# Revit family: Dimension Lumber
name_source: partatom
category: Structural Framing
revit_build: Autodesk Revit Architecture 2012 (Build: 20110210_1515)
units: mm (PartAtom-declared; Revit-internal decimal feet)

## types (24) — shared parameters
Assembly Code = B10

## per-type parameters (varying)
| type | A | b | d |
| 2x3 | 3.75 in² | 0' - 1 1/2" | 0' - 2 1/2" |
| 2x4 | 5.25 in² | 0' - 1 1/2" | 0' - 3 1/2" |
| 2x5 | 6.75 in² | 0' - 1 1/2" | 0' - 4 1/2" |
| 2x6 | 8.25 in² | 0' - 1 1/2" | 0' - 5 1/2" |
| 2x8 | 10.88 in² | 0' - 1 1/2" | 0' - 7 1/4" |
| 2x10 | 13.88 in² | 0' - 1 1/2" | 0' - 9 1/4" |
| 2x12 | 16.88 in² | 0' - 1 1/2" | 0' - 11 1/4" |
| 2x14 | 19.88 in² | 0' - 1 1/2" | 1' - 1 1/4" |
| 3x4 | 8.75 in² | 0' - 2 1/2" | 0' - 3 1/2" |
| 3x5 | 11.25 in² | 0' - 2 1/2" | 0' - 4 1/2" |
| 3x6 | 13.75 in² | 0' - 2 1/2" | 0' - 5 1/2" |
| 3x8 | 18.13 in² | 0' - 2 1/2" | 0' - 7 1/4" |
| 3x10 | 23.13 in² | 0' - 2 1/2" | 0' - 9 1/4" |
| 3x12 | 28.13 in² | 0' - 2 1/2" | 0' - 11 1/4" |
| 3x14 | 33.13 in² | 0' - 2 1/2" | 1' - 1 1/4" |
| 3x16 | 38.13 in² | 0' - 2 1/2" | 1' - 3 1/4" |
| 4x4 | 12.25 in² | 0' - 3 1/2" | 0' - 3 1/2" |
| 4x5 | 15.75 in² | 0' - 3 1/2" | 0' - 4 1/2" |
| 4x6 | 19.25 in² | 0' - 3 1/2" | 0' - 5 1/2" |
| 4x8 | 25.38 in² | 0' - 3 1/2" | 0' - 7 1/4" |
| 4x10 | 32.38 in² | 0' - 3 1/2" | 0' - 9 1/4" |
| 4x12 | 39.38 in² | 0' - 3 1/2" | 0' - 11 1/4" |
| 4x14 | 47.25 in² | 0' - 3 1/2" | 1' - 1 1/4" |
| 4x16 | 54.25 in² | 0' - 3 1/2" | 1' - 3 1/4" |

## geometry (parser evidence)
native form markers: Sweep x2
no freeform markers — native parametric forms only
